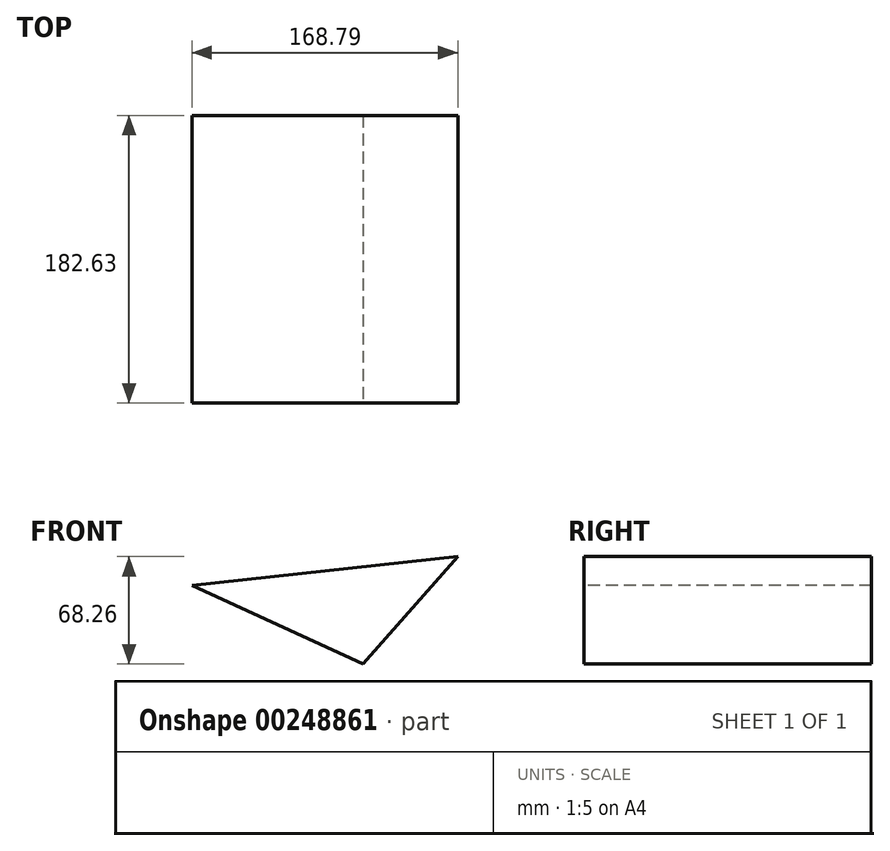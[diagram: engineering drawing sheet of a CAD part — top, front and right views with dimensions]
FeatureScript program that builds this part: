
annotation { "Feature Type Name" : "Feature", "Feature Type Description" : "" }
export const myFeature = defineFeature(function(context is Context, id is Id, definition is map)
    precondition{}
    {
        {
            var Q0;
            Q0=qCreatedBy(makeId("Front.planeOp"),FACE);
            var sketch = newSketch(context, id + "F0", { "sketchPlane" : qUnion([Q0])});
            skLineSegment(sketch, "E0", {"start": v(-77.8, 0) * mm, "end": v(30.82, -50.06) * mm});
            skLineSegment(sketch, "E1", {"start": v(30.82, -50.06) * mm, "end": v(91, 18.2) * mm});
            skLineSegment(sketch, "E2", {"start": v(91, 18.2) * mm, "end": v(-77.8, 0) * mm});
            skSolve(sketch);
        }
        {
            var Q0;
            Q0=makeQuery(id+"F0.imprint","IMPRINT",FACE,{"disambiguationData":[TD([[makeQuery(id+"F0.imprint","IMPRINT",EDGE,{"derivedFrom":sQuery(id+"F0.wireOp",EDGE,"E0")}),1.0]])]});
            extrude(context, id + "F1", {"entities" : qUnion([Q0]), "oppositeDirection" : true, "depth" : 182.63 * mm});
        }
    });
